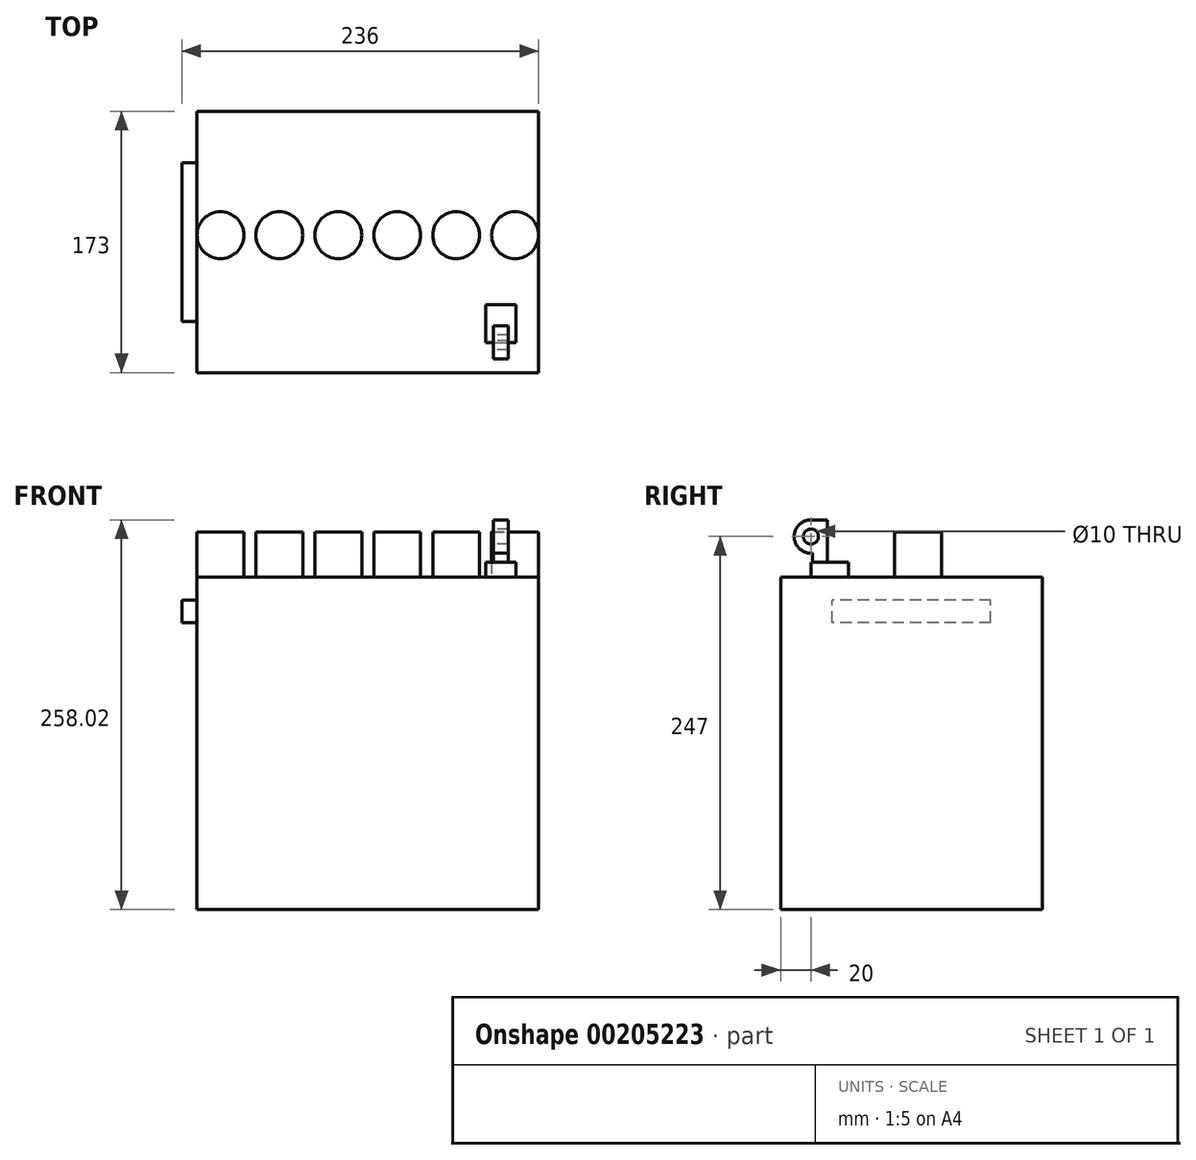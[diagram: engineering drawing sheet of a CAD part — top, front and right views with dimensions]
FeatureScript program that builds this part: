
annotation { "Feature Type Name" : "Feature", "Feature Type Description" : "" }
export const myFeature = defineFeature(function(context is Context, id is Id, definition is map)
    precondition{}
    {
        {
            var Q0;
            Q0=qCreatedBy(makeId("Top.planeOp"),FACE);
            var sketch = newSketch(context, id + "F0", { "sketchPlane" : qUnion([Q0])});
            skLineSegment(sketch, "E0.bottom", {"start": v(-113, 86.5) * mm, "end": v(113, 86.5) * mm});
            skLineSegment(sketch, "E0.top", {"start": v(-113, -86.5) * mm, "end": v(113, -86.5) * mm});
            skLineSegment(sketch, "E0.left", {"start": v(-113, 86.5) * mm, "end": v(-113, -86.5) * mm});
            skLineSegment(sketch, "E0.right", {"start": v(113, 86.5) * mm, "end": v(113, -86.5) * mm});
            skPoint(sketch, "E0.middle", {"position": v(0, 0) * mm});
            skSolve(sketch);
        }
        {
            var Q0;
            Q0=makeQuery(id+"F0.imprint","IMPRINT",FACE,{"disambiguationData":[TD([[makeQuery(id+"F0.imprint","IMPRINT",EDGE,{"derivedFrom":sQuery(id+"F0.wireOp",EDGE,"E0.bottom")}),-1.0]])]});
            extrude(context, id + "F1", {"entities" : qUnion([Q0]), "endBound" : BoundingType.SYMMETRIC, "depth" : 220 * mm});
        }
        {
            var Q0;
            Q0=makeQuery(id+"F1.opExtrude","SWEPT_FACE",FACE,{"disambiguationData":[OSD([sQuery(id+"F0.wireOp",EDGE,"E0.left")])]});
            var sketch = newSketch(context, id + "F2", { "sketchPlane" : qUnion([Q0])});
            skLineSegment(sketch, "E1.bottom", {"start": v(-52.5, 80) * mm, "end": v(52.5, 80) * mm});
            skLineSegment(sketch, "E1.top", {"start": v(-52.5, 95) * mm, "end": v(52.5, 95) * mm});
            skLineSegment(sketch, "E1.left", {"start": v(-52.5, 80) * mm, "end": v(-52.5, 95) * mm});
            skLineSegment(sketch, "E1.right", {"start": v(52.5, 80) * mm, "end": v(52.5, 95) * mm});
            skPoint(sketch, "E1.middle", {"position": v(0, 87.5) * mm});
            skSolve(sketch);
        }
        {
            var Q0;
            Q0=makeQuery(id+"F2.imprint","IMPRINT",FACE,{"disambiguationData":[TD([[makeQuery(id+"F2.imprint","IMPRINT",EDGE,{"derivedFrom":sQuery(id+"F2.wireOp",EDGE,"E1.bottom")}),1.0]])]});
            extrude(context, id + "F3", {"entities" : qUnion([Q0]), "operationType" : NewBodyOperationType.ADD, "depth" : 10 * mm});
        }
        {
            var Q0;
            Q0=makeQuery(id+"F1.opExtrude","CAP_FACE",FACE,{"disambiguationData":[OSD([sQuery(id+"F0.wireOp",EDGE,"E0.bottom"),sQuery(id+"F0.wireOp",EDGE,"E0.top"),sQuery(id+"F0.wireOp",EDGE,"E0.left"),sQuery(id+"F0.wireOp",EDGE,"E0.right")])],"isStart":false});
            var sketch = newSketch(context, id + "F4", { "sketchPlane" : qUnion([Q0])});
            skLineSegment(sketch, "E2", {"start": v(-173.35, 4.5) * mm, "end": v(127.4, 4.5) * mm, "construction": true});
            skCircle(sketch, "E3", {"center": v(97.5, 4.5) * mm, "radius": 15.5 * mm});
            skCircle(sketch, "E4", {"center": v(58.5, 4.5) * mm, "radius": 15.5 * mm});
            skCircle(sketch, "E5", {"center": v(-19.5, 4.5) * mm, "radius": 15.5 * mm});
            skCircle(sketch, "E6", {"center": v(-58.5, 4.5) * mm, "radius": 15.5 * mm});
            skCircle(sketch, "E7", {"center": v(-97.5, 4.5) * mm, "radius": 15.5 * mm});
            skLineSegment(sketch, "E8", {"start": v(0, 86.5) * mm, "end": v(0, -86.5) * mm, "construction": true});
            skCircle(sketch, "E9", {"center": v(19.5, 4.5) * mm, "radius": 15.5 * mm});
            skSolve(sketch);
        }
        {
            var Q0;
            Q0=makeQuery(id+"F4.imprint","IMPRINT",FACE,{"disambiguationData":[TD([[makeQuery(id+"F4.imprint","IMPRINT",EDGE,{"derivedFrom":sQuery(id+"F4.wireOp",EDGE,"E7")}),1.0]])]});
            var Q1;
            Q1=makeQuery(id+"F4.imprint","IMPRINT",FACE,{"disambiguationData":[TD([[makeQuery(id+"F4.imprint","IMPRINT",EDGE,{"derivedFrom":sQuery(id+"F4.wireOp",EDGE,"E6")}),1.0]])]});
            var Q2;
            Q2=makeQuery(id+"F4.imprint","IMPRINT",FACE,{"disambiguationData":[TD([[makeQuery(id+"F4.imprint","IMPRINT",EDGE,{"derivedFrom":sQuery(id+"F4.wireOp",EDGE,"E5")}),1.0]])]});
            var Q3;
            Q3=makeQuery(id+"F4.imprint","IMPRINT",FACE,{"disambiguationData":[TD([[makeQuery(id+"F4.imprint","IMPRINT",EDGE,{"derivedFrom":sQuery(id+"F4.wireOp",EDGE,"E9")}),1.0]])]});
            var Q4;
            Q4=makeQuery(id+"F4.imprint","IMPRINT",FACE,{"disambiguationData":[TD([[makeQuery(id+"F4.imprint","IMPRINT",EDGE,{"derivedFrom":sQuery(id+"F4.wireOp",EDGE,"E4")}),1.0]])]});
            var Q5;
            Q5=makeQuery(id+"F4.imprint","IMPRINT",FACE,{"disambiguationData":[TD([[makeQuery(id+"F4.imprint","IMPRINT",EDGE,{"derivedFrom":sQuery(id+"F4.wireOp",EDGE,"E3")}),1.0]])]});
            extrude(context, id + "F5", {"entities" : qUnion([Q0, Q1, Q2, Q3, Q4, Q5]), "operationType" : NewBodyOperationType.ADD, "depth" : 30 * mm});
        }
        {
            var Q0;
            Q0=makeQuery(id+"F1.opExtrude","CAP_FACE",FACE,{"disambiguationData":[OSD([sQuery(id+"F0.wireOp",EDGE,"E0.bottom"),sQuery(id+"F0.wireOp",EDGE,"E0.top"),sQuery(id+"F0.wireOp",EDGE,"E0.left"),sQuery(id+"F0.wireOp",EDGE,"E0.right")])],"isStart":false});
            var sketch = newSketch(context, id + "F6", { "sketchPlane" : qUnion([Q0])});
            skLineSegment(sketch, "E10", {"start": v(88, -121.7) * mm, "end": v(88, -5.57) * mm, "construction": true});
            skLineSegment(sketch, "E11.bottom", {"start": v(78, -66.5) * mm, "end": v(98, -66.5) * mm});
            skLineSegment(sketch, "E11.top", {"start": v(78, -41.5) * mm, "end": v(98, -41.5) * mm});
            skLineSegment(sketch, "E11.left", {"start": v(78, -66.5) * mm, "end": v(78, -41.5) * mm});
            skLineSegment(sketch, "E11.right", {"start": v(98, -66.5) * mm, "end": v(98, -41.5) * mm});
            skPoint(sketch, "E11.middle", {"position": v(88, -54) * mm});
            skSolve(sketch);
        }
        {
            var Q0;
            Q0=makeQuery(id+"F6.imprint","IMPRINT",FACE,{"disambiguationData":[TD([[makeQuery(id+"F6.imprint","IMPRINT",EDGE,{"derivedFrom":sQuery(id+"F6.wireOp",EDGE,"E11.bottom")}),1.0]])]});
            extrude(context, id + "F7", {"entities" : qUnion([Q0]), "operationType" : NewBodyOperationType.ADD, "depth" : 10 * mm});
        }
        {
            var Q0;
            Q0=makeQuery(id+"F7.opExtrude","CAP_EDGE",EDGE,{"disambiguationData":[OSD([sQuery(id+"F6.wireOp",EDGE,"E11.bottom")])],"isStart":false});
            cPoint(context, id + "F8", {"entities" : qUnion([Q0]), "parameter" : 0.5});
        }
        {
            var Q0;
            Q0=makeQuery(id+"F1.opExtrude","SWEPT_FACE",FACE,{"disambiguationData":[OSD([sQuery(id+"F0.wireOp",EDGE,"E0.right")])]});
            var Q1;
            Q1 = qCreatedBy(id + "F8" ,VERTEX);
            cPlane(context, id + "F9", {"entities" : qUnion([Q0, Q1]), "cplaneType" : CPlaneType.PLANE_POINT, "offset" : 25 * mm, "width" : 150 * mm, "height" : 150 * mm});
        }
        {
            var Q0;
            Q0=qCreatedBy(id+"F9.planeOp",FACE);
            var sketch = newSketch(context, id + "F10", { "sketchPlane" : qUnion([Q0])});
            skCircle(sketch, "E12", {"center": v(-66.5, 137) * mm, "radius": 5 * mm});
            skArc(sketch, "E13", {"start": v(-66.5, 148.02) * mm, "mid": v(-77.51, 136.49) * mm, "end": v(-65.48, 126.02) * mm});
            skLineSegment(sketch, "E14", {"start": v(-66.5, 148.02) * mm, "end": v(-55.48, 148.02) * mm});
            skLineSegment(sketch, "E15", {"start": v(-55.48, 148.02) * mm, "end": v(-55.48, 137) * mm});
            skLineSegment(sketch, "E16", {"start": v(-65.48, 126.02) * mm, "end": v(-65.48, 120) * mm});
            skLineSegment(sketch, "E17", {"start": v(-55.48, 137) * mm, "end": v(-55.48, 120) * mm});
            skLineSegment(sketch, "E18", {"start": v(-55.48, 120) * mm, "end": v(-65.48, 120) * mm});
            skSolve(sketch);
        }
        {
            var Q0;
            Q0=makeQuery(id+"F10.imprint","IMPRINT",FACE,{"disambiguationData":[TD([[makeQuery(id+"F10.imprint","IMPRINT",EDGE,{"derivedFrom":sQuery(id+"F10.wireOp",EDGE,"E12")}),-1.0]])]});
            extrude(context, id + "F11", {"entities" : qUnion([Q0]), "operationType" : NewBodyOperationType.ADD, "endBound" : BoundingType.SYMMETRIC, "depth" : 10 * mm});
        }
    });
